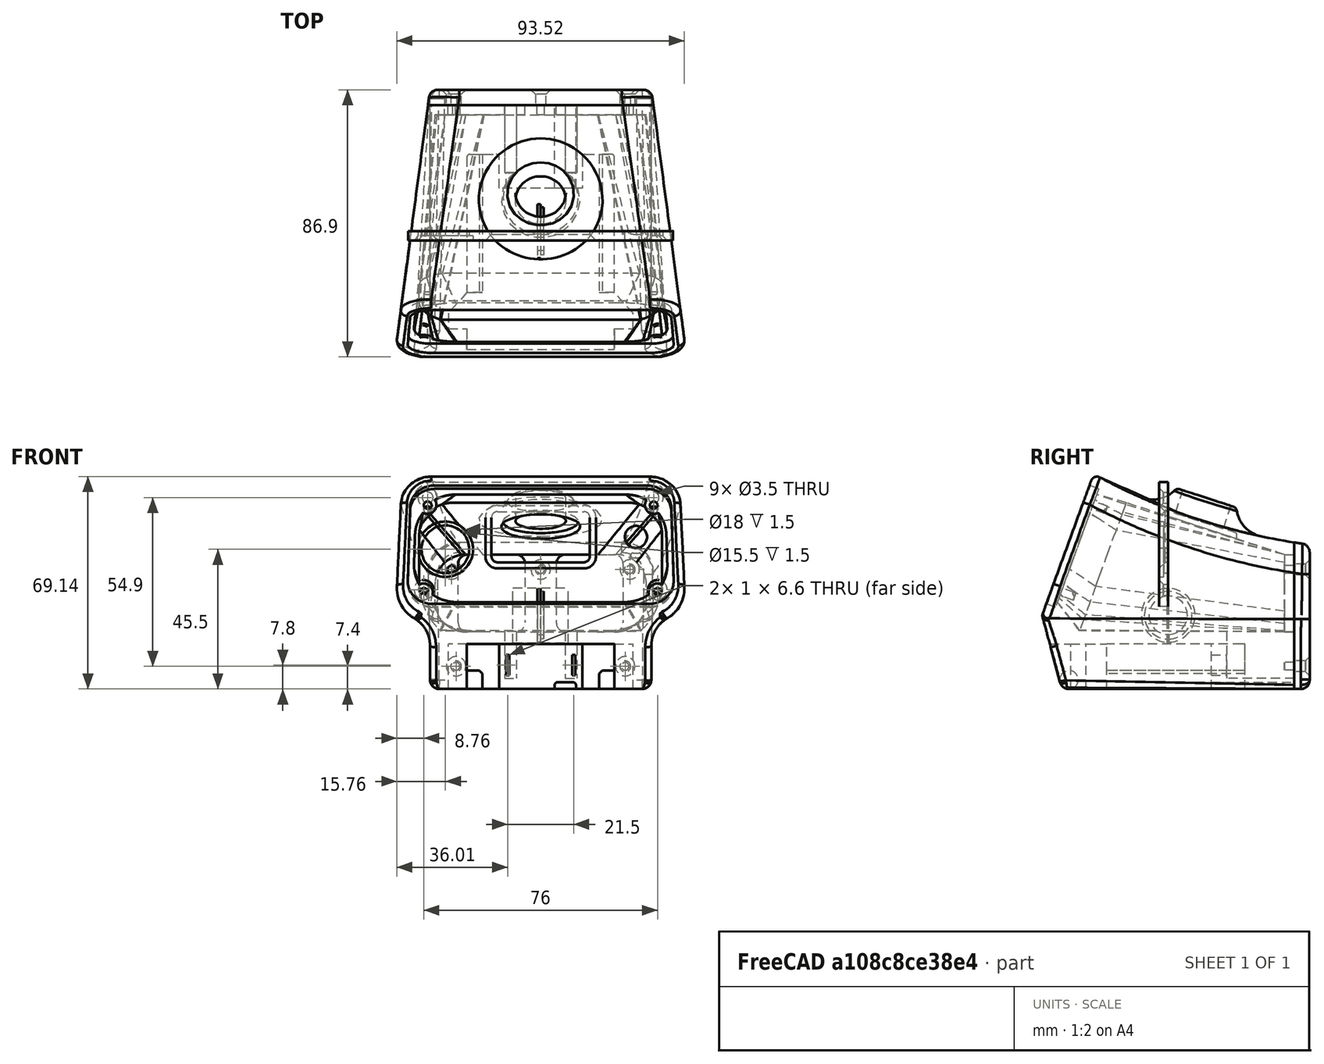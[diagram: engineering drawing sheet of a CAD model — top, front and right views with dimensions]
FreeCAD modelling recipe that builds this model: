
FCSTD DOCUMENT  (FreeCAD 2021.412R24301 +3461 (Git))
Label: solder_station5
License: All rights reserved
LicenseURL: http://en.wikipedia.org/wiki/All_rights_reserved
objects: Sketcher::SketchObject×21, PartDesign::Pocket×10, Part::FeaturePython×6, PartDesign::Fillet×6, App::DocumentObjectGroup×4, PartDesign::Body×4, Mesh::Feature×4, PartDesign::Chamfer×3, PartDesign::FeatureBase×2, PartDesign::Pad×2, PartDesign::Revolution×2, Spreadsheet::Sheet×1, Part::Plane×1, Part::Loft×1, Part::Extrusion×1, Part::MultiCommon×1, PartDesign::SubtractiveLoft×1, PartDesign::Groove×1, Part::Box×1, App::Part×1
note: 115 computed .brp shape members not serialized (recipe doc carries the construction recipe); baked Part::Feature solids carry a one-line shape summary decoded from their .brp

FEATURE [Sketcher::SketchObject] Sketch  label="RearSupport"
  AttachmentOffset = pos=(0,0,-37.8) rot=(0,0,1;0rad)
  FullyConstrained = true
  MapMode = 5
  Placement = pos=(0,37.8,8.4e-15) rot=(1,0,0;1.5708rad)
  Support = -> [XZ_Plane005]
  expr: .AttachmentOffset.Base.z = -<<param>>.mid_depth / 2 + <<param>>.wall
  expr: .Constraints[24] = 3
  expr: .Constraints[37] = <<param>>.bottom_height
  expr: .Constraints[38] = <<param>>.floor
  expr: .Constraints[39] = <<param>>.rear_height - <<param>>.wall
  expr: .Constraints[47] = <<param>>.reart_screw_width2
  expr: .Constraints[48] = <<param>>.rear_screw_width1
  expr: .Constraints[49] = <<param>>.screw_hole
  expr: .Constraints[50] = <<param>>.rear_screw_height
  expr: .Constraints[51] = <<param>>.rear_screw_height
  expr: .Constraints[52] = <<param>>.rear_screw_offset
  sketch-geometry (22):
    g0: LineSegment StartX=-23.8 StartY=19.8 StartZ=0 EndX=-8.1 EndY=19.8 EndZ=0
    g1: LineSegment StartX=26.8 StartY=16.8 StartZ=0 EndX=26.8 EndY=-2.4 EndZ=0
    g2: LineSegment StartX=23.8 StartY=-5.4 StartZ=0 EndX=8.1 EndY=-5.4 EndZ=0
    g3: LineSegment StartX=-26.8 StartY=-2.4 StartZ=0 EndX=-26.8 EndY=16.8 EndZ=0
    g4: LineSegment StartX=-5.1 StartY=16.8 StartZ=0 EndX=-5.1 EndY=-2.4 EndZ=0
    g5: LineSegment StartX=5.1 StartY=16.8 StartZ=0 EndX=5.1 EndY=-2.4 EndZ=0
    g6: LineSegment StartX=8.1 StartY=19.8 StartZ=0 EndX=23.8 EndY=19.8 EndZ=0
    g7: LineSegment StartX=-8.1 StartY=-5.4 StartZ=0 EndX=-23.8 EndY=-5.4 EndZ=0
    g8: ArcOfCircle CenterX=-8.1 CenterY=16.8 CenterZ=0 NormalX=0 NormalY=0 NormalZ=1 AngleXU=0 Radius=3 StartAngle=0 EndAngle=1.5708
    g9: ArcOfCircle CenterX=8.1 CenterY=16.8 CenterZ=0 NormalX=0 NormalY=0 NormalZ=1 AngleXU=0 Radius=3 StartAngle=1.5708 EndAngle=3.14159
    g10: ArcOfCircle CenterX=-8.1 CenterY=-2.4 CenterZ=0 NormalX=0 NormalY=0 NormalZ=1 AngleXU=0 Radius=3 StartAngle=4.71239 EndAngle=6.28319
    g11: ArcOfCircle CenterX=8.1 CenterY=-2.4 CenterZ=0 NormalX=0 NormalY=0 NormalZ=1 AngleXU=0 Radius=3 StartAngle=3.14159 EndAngle=4.71239
    g12: ArcOfCircle CenterX=-23.8 CenterY=16.8 CenterZ=0 NormalX=0 NormalY=0 NormalZ=1 AngleXU=0 Radius=3 StartAngle=1.5708 EndAngle=3.14159
    g13: ArcOfCircle CenterX=-23.8 CenterY=-2.4 CenterZ=0 NormalX=0 NormalY=0 NormalZ=1 AngleXU=0 Radius=3 StartAngle=3.14159 EndAngle=4.71239
    g14: ArcOfCircle CenterX=23.8 CenterY=16.8 CenterZ=0 NormalX=0 NormalY=0 NormalZ=1 AngleXU=0 Radius=3 StartAngle=3e-16 EndAngle=1.5708
    g15: ArcOfCircle CenterX=23.8 CenterY=-2.4 CenterZ=0 NormalX=0 NormalY=0 NormalZ=1 AngleXU=0 Radius=3 StartAngle=4.71239 EndAngle=6.28319
    g16: Circle [constr] CenterX=0 CenterY=-24 CenterZ=0 NormalX=0 NormalY=0 NormalZ=1 AngleXU=0 Radius=3
    g17: Circle CenterX=0 CenterY=14.9 CenterZ=0 NormalX=0 NormalY=0 NormalZ=1 AngleXU=0 Radius=1.25
    g18: Circle CenterX=-29 CenterY=14.9 CenterZ=0 NormalX=0 NormalY=0 NormalZ=1 AngleXU=0 Radius=1.25
    g19: Circle CenterX=-27.5 CenterY=-16.6 CenterZ=0 NormalX=0 NormalY=0 NormalZ=1 AngleXU=0 Radius=1.25
    g20: Circle CenterX=27.5 CenterY=-16.6 CenterZ=0 NormalX=0 NormalY=0 NormalZ=1 AngleXU=0 Radius=1.25
    g21: Circle CenterX=29 CenterY=14.9 CenterZ=0 NormalX=0 NormalY=0 NormalZ=1 AngleXU=0 Radius=1.25
  constraints (53):
    c: Horizontal(g0)
    c: Horizontal(g2)
    c: Vertical(g1)
    c: Vertical(g3)
    c: Vertical(g4)
    c: Vertical(g5)
    c: Tangent(g0,g6)
    c: Tangent(g2,g7)
    c: Tangent(g0,g8) = 1.5708
    c: Tangent(g4,g8) = 1.5708
    c: Tangent(g5,g9) = -1.5708
    c: Tangent(g6,g9) = 1.5708
    c: Tangent(g7,g10) = 1.5708
    c: Tangent(g4,g10) = 1.5708
    c: Tangent(g5,g11) = -1.5708
    c: Tangent(g2,g11) = 1.5708
    c: Tangent(g0,g12) = 1.5708
    c: Tangent(g3,g12) = 1.5708
    c: Tangent(g3,g13) = 1.5708
    c: Tangent(g7,g13) = 1.5708
    c: Tangent(g6,g14) = 1.5708
    c: Tangent(g1,g14) = 1.5708
    c: Tangent(g1,g15) = 1.5708
    c: Tangent(g2,g15) = 1.5708
    c: Radius(g9) = 3
    c: Equal(g12,g13)
    c: Equal(g13,g10)
    c: Equal(g10,g8)
    c: Equal(g11,g15)
    c: Equal(g15,g14)
    c: Equal(g14,g9)
    c: DistanceX(g4,g-1) = 5.1
    c: DistanceX(g5,g1) = 21.7
    c: Symmetric(g4,g5,g-2)
    c: Equal(g7,g2)
    c: PointOnObject(g16,g-2)
    c: Radius(g16) = 3
    c: DistanceY(g16,g-1) = 24
    c: DistanceY(g16,g2) = 18.6
    c: DistanceY(g16,g6) = 43.8
    c: PointOnObject(g17,g-2)
    c: Equal(g21,g18)
    c: Equal(g18,g19)
    c: Equal(g19,g20)
    c: Equal(g18,g17)
    c: Symmetric(g20,g19,g-2)
    c: Symmetric(g18,g21,g-2)
    c: DistanceX(g19,g20) = 55
    c: DistanceX(g18,g21) = 58
    c: Diameter(g19) = 2.5
    c: DistanceY(g20,g21) = 31.5
    c: DistanceY(g20,g17) = 31.5
    c: DistanceY(g16,g19) = 7.4
FEATURE [Spreadsheet::Sheet] Spreadsheet  label="param"
  PythonMode = false
  cells = A1=Body; B2=top_depth; C2(top_depth)=70; B3=mid_depth; C3(mid_depth)=82; D3=half is rear reference; B4=bottom_depth; C4(bottom_depth)=75; B6=bottom_width; C6(bottom_width)=72; B7=bottom_height; C7(bottom_height)=24; B8=bottom_angle; C8(bottom_angle)=15; B10=rear_width; C10(rear_width)=72; B11=rear_height; C11(rear_height)=47; F11=41; B13=mid_width; C13(mid_width)=80; B14=mid_height; C14(mid_height)=56; F14=50; B16=front_width1; C16(front_width1)=92; D16=@top; E16=upper; F16=91; B17=front_width2; C17(front_width2)=95; D17=@mid; E17=lower; F17=94; B18=front_height; C18(front_height)=70; F18=64; B19=front_angle; C19(front_angle)=20; B21=wall; C21(wall)=3.2; B22=radius_big; C22(radius_big)=10; B23=radius_small; C23(radius_small)=3; B24=arch; C24(arch)=200; A26=Button; B27=button_offset; C27(button_offset)=10; B28=button_inside_dia; C28(button_inside_dia)=20; B29=button_outside_dia; C29(button_outside_dia)=22; B30=button_height; C30(button_height)=30.6; F30=26; B31=button_extension; C31(button_extension)=8; B32=button_fillet; C32(button_fillet)=12; B33=button_angle; C33(button_angle)=-18; F33=-17; B34=button_hole; C34(button_hole)=16.4; B35=button_hole_center; C35(button_hole_center)=-0.5; A37=Battery Cuts; B38=batt_carveout; C38(batt_carveout)=14.6; B39=batt_rail; C39(batt_rail)=6; B40=batt_rail_length; C40(batt_rail_length)=45; A42=Terminals; B43=terminal_height; C43(terminal_height)=6.6; B44=terminal_thickness; C44(terminal_thickness)=1; B45=terminal_seperation; C45(terminal_seperation)=21.5; B46=terminal_offset; C46(terminal_offset)=4.5; B47=terminal_depth; C47(terminal_depth)=22; A49=Box Interior; B50=floor; C50(floor)=18.6; B51=rear_inside_width; C51(rear_inside_width)==C10 - C21; D51=calc; B52=rear_inside_height; C52(rear_inside_height)==C11 - C21; D52=calc; B53=mid_inside_width; C53(mid_inside_width)==C13; D53=calc; B54=mid_inside_height; C54(mid_inside_height)==C14 + 7; D54=calc; F54=6; B55=front_inside_width1; C55(front_inside_width1)==C62 - C58 * 2; D55=calc; E55=upper; B56=front_inside_width2; C56(front_inside_width2)==C63 - C58 * 2; D56=calc; E56=lower; B57=front_inside_height; C57(front_inside_height)==C64 - C59 * 2; D57=calc; B58=front_width_lip_width; C58(front_width_lip_width)=3; B59=front_inside_lip_height; C59(front_inside_lip_height)=2; A61=Face; B62=face_width1; C62(face_width1)==84 + 1; B63=face_width2; C63(face_width2)==85.5 + 1; B64=face_height; C64(face_height)=41; F64=35; B65=face_thickness; C65(face_thickness)=3; B66=face_radius; C66(face_radius)=8; B67=face_offset; C67(face_offset)=2.8; F67=2.8; A69=Screws; B70=screw_hole; C70(screw_hole)=2.5; B72=front_screw_width1; C72(front_screw_width1)=73.5; D72=upper; B73=front_screw_width2; C73(front_screw_width2)=76; D73=lower; B74=front_screw_height; C74(front_screw_height)=30; F74=24; B75=front_screw_offset; C75(front_screw_offset)=5.5; B77=rear_screw_width1; C77(rear_screw_width1)=58; B78=reart_screw_width2; C78(reart_screw_width2)=55; B79=rear_screw_height; C79(rear_screw_height)=31.5; F79=25.5; B80=rear_screw_offset; C80(rear_screw_offset)=7.4; A82=Back; B83=back_thickness; C83(back_thickness)=5
FEATURE [Sketcher::SketchObject] Sketch008  label="SketchButtonHole"
  AttachmentOffset = pos=(0,-0.5,30.6) rot=(1,0,0;-0.314159rad)
  FullyConstrained = true
  MapMode = 5
  Placement = pos=(0,-0.5,30.6) rot=(1,0,0;5.96903rad)
  Support = -> [XY_Plane005]
  expr: .AttachmentOffset.Base.y = <<param>>.button_hole_center
  expr: .AttachmentOffset.Base.z = <<param>>.button_height
  expr: .AttachmentOffset.Rotation.Angle = <<param>>.button_angle
  expr: .Constraints[0] = <<param>>.button_hole
  expr: .Constraints[2] = <<param>>.button_offset
  sketch-geometry (1):
    g0: Circle CenterX=0 CenterY=10 CenterZ=0 NormalX=0 NormalY=0 NormalZ=1 AngleXU=0 Radius=8.2
  constraints (3):
    c: Diameter(g0) = 16.4
    c: PointOnObject(g0,g-2)
    c: DistanceY(g-1,g0) = 10
FEATURE [Sketcher::SketchObject] Sketch012  label="SketchSide"
  AttachmentOffset = pos=(2.5,0,0) rot=(0,0,1;0rad)
  FullyConstrained = true
  MapMode = 5
  Placement = pos=(6e-16,2.5,-6e-16) rot=(0.57735,0.57735,0.57735;2.0944rad)
  Support = -> [YZ_Plane006]
  expr: .AttachmentOffset.Base.x = <<param>>.back_thickness / 2
  expr: .Constraints[14] = <<param>>.bottom_height
  expr: .Constraints[15] = <<param>>.radius_small
  expr: .Constraints[16] = 90 - <<param>>.bottom_angle
  expr: .Constraints[17] = 90 - <<param>>.front_angle
  expr: .Constraints[21] = <<param>>.front_height
  expr: .Constraints[4] = <<param>>.rear_height - <<param>>.bottom_height
  expr: .Constraints[5] = <<param>>.arch
  expr: .Constraints[6] = <<param>>.mid_depth + <<param>>.back_thickness
  sketch-geometry (7):
    g0: LineSegment StartX=43.5 StartY=0 StartZ=0 EndX=43.5 EndY=23 EndZ=0
    g1: LineSegment StartX=-43.5 StartY=0 StartZ=0 EndX=-26.7574 EndY=46 EndZ=0
    g2: ArcOfCircle CenterX=69.5235 CenterY=221.3 CenterZ=0 NormalX=0 NormalY=0 NormalZ=1 AngleXU=0 Radius=200 StartAngle=4.21013 EndAngle=4.5819
    g3: LineSegment StartX=-43.5 StartY=0 StartZ=0 EndX=-37.665 EndY=-21.7765 EndZ=0
    g4: LineSegment StartX=-34.7673 StartY=-24 StartZ=0 EndX=43.5 EndY=-24 EndZ=0
    g5: LineSegment StartX=43.5 StartY=-24 StartZ=0 EndX=43.5 EndY=0 EndZ=0
    g6: ArcOfCircle CenterX=-34.7672 CenterY=-21 CenterZ=0 NormalX=0 NormalY=0 NormalZ=1 AngleXU=0 Radius=3 StartAngle=3.4034 EndAngle=4.71238
  constraints (22):
    c: PointOnObject(g1,g-1)
    c: Vertical(g0)
    c: Coincident(g2,g0)
    c: Symmetric(g1,g0,g-2)
    c: DistanceY(g0,g0) = 23
    c: Radius(g2) = 200
    c: DistanceX(g1,g0) = 87
    c: Horizontal(g4)
    c: Coincident(g5,g4)
    c: Vertical(g5)
    c: Coincident(g6,g3)
    c: Coincident(g6,g4)
    c: Tangent(g6,g4)
    c: Tangent(g6,g3)
    c: DistanceY(g4,g-1) = 24
    c: Radius(g6) = 3
    c: Angle(g3,g-1) = 1.309
    c: Angle(g-1,g1) = 1.22173
    c: Coincident(g3,g1)
    c: Coincident(g5,g0)
    c: Coincident(g2,g1)
    c: DistanceY(g4,g1) = 70
FEATURE [Sketcher::SketchObject] Sketch018  label="SketchBat1"
  AttachmentOffset = pos=(0,0,-24) rot=(0,0,1;0rad)
  FullyConstrained = true
  MapMode = 5
  Placement = pos=(0,0,-24) rot=(0,0,1;0rad)
  Support = -> [XY_Plane005]
  expr: .AttachmentOffset.Base.z = -<<param>>.bottom_height
  expr: .Constraints[63] = <<param>>.batt_rail_length
  expr: .Constraints[64] = <<param>>.mid_depth / 2
  sketch-geometry (21):
    g0: LineSegment StartX=-24 StartY=-41.7082 StartZ=0 EndX=24 EndY=-41.7082 EndZ=0
    g1: LineSegment StartX=24 StartY=-41.7082 StartZ=0 EndX=24 EndY=-31.7082 EndZ=0
    g2: LineSegment StartX=24 StartY=-31.7082 StartZ=0 EndX=30 EndY=-31.7082 EndZ=0
    g3: LineSegment StartX=30 StartY=-31.7082 StartZ=0 EndX=30 EndY=-26.7082 EndZ=0
    g4: LineSegment StartX=30 StartY=-26.7082 StartZ=0 EndX=24 EndY=-20 EndZ=0
    g5: LineSegment StartX=24 StartY=-20 StartZ=0 EndX=24 EndY=24 EndZ=0
    g6: LineSegment StartX=13.5 StartY=24 StartZ=0 EndX=13.5 EndY=14 EndZ=0
    g7: LineSegment StartX=13.5 StartY=14 StartZ=0 EndX=-13.5 EndY=14 EndZ=0
    g8: LineSegment StartX=-13.5 StartY=14 StartZ=0 EndX=-13.5 EndY=24 EndZ=0
    g9: LineSegment StartX=-24 StartY=24 StartZ=0 EndX=-24 EndY=-20 EndZ=0
    g10: LineSegment StartX=-24 StartY=-20 StartZ=0 EndX=-30 EndY=-26.7082 EndZ=0
    g11: LineSegment StartX=-30 StartY=-26.7082 StartZ=0 EndX=-30 EndY=-31.7082 EndZ=0
    g12: LineSegment StartX=-30 StartY=-31.7082 StartZ=0 EndX=-24 EndY=-31.7082 EndZ=0
    g13: LineSegment StartX=-24 StartY=-31.7082 StartZ=0 EndX=-24 EndY=-41.7082 EndZ=0
    g14: Circle [constr] CenterX=0 CenterY=41 CenterZ=0 NormalX=0 NormalY=0 NormalZ=1 AngleXU=0 Radius=4
    g15: ArcOfCircle CenterX=-14.5 CenterY=24 CenterZ=0 NormalX=0 NormalY=0 NormalZ=1 AngleXU=0 Radius=1 StartAngle=6.28318 EndAngle=7.85399
    g16: LineSegment StartX=-23 StartY=25 StartZ=0 EndX=-14.5 EndY=25 EndZ=0
    g17: LineSegment StartX=14.5 StartY=25 StartZ=0 EndX=23 EndY=25 EndZ=0
    g18: ArcOfCircle CenterX=-23 CenterY=24 CenterZ=0 NormalX=0 NormalY=0 NormalZ=1 AngleXU=0 Radius=1 StartAngle=1.57079 EndAngle=3.1416
    g19: ArcOfCircle CenterX=14.5 CenterY=24 CenterZ=0 NormalX=0 NormalY=0 NormalZ=1 AngleXU=0 Radius=1 StartAngle=1.5708 EndAngle=3.14159
    g20: ArcOfCircle CenterX=23 CenterY=24 CenterZ=0 NormalX=0 NormalY=0 NormalZ=1 AngleXU=0 Radius=1.00001 StartAngle=2.75124e-06 EndAngle=1.5708
  constraints (65):
    c: Horizontal(g0)
    c: Coincident(g1,g0)
    c: Vertical(g1)
    c: Coincident(g2,g1)
    c: Horizontal(g2)
    c: Coincident(g3,g2)
    c: Coincident(g3,g4)
    c: Vertical(g5)
    c: Coincident(g6,g7)
    c: Coincident(g7,g8)
    c: Vertical(g8)
    c: Vertical(g9)
    c: Coincident(g10,g11)
    c: Vertical(g11)
    c: Coincident(g11,g12)
    c: Horizontal(g12)
    c: Coincident(g12,g13)
    c: Equal(g6,g8)
    c: Equal(g5,g9)
    c: Equal(g4,g10)
    c: Equal(g3,g11)
    c: Equal(g12,g2)
    c: Equal(g1,g13)
    c: Coincident(g13,g0)
    c: Vertical(g13)
    c: DistanceX(g7,g7) = 27
    c: Symmetric(g7,g6,g-2)
    c: Distance(g4) = 9
    c: Vertical(g3)
    c: DistanceY(g3,g3) = 5
    c: DistanceX(g2,g2) = 6
    c: DistanceY(g1,g1) = 10
    c: DistanceX(g0,g0) = 48
    c: PointOnObject(g14,g-2)
    c: Coincident(g9,g10)
    c: Coincident(g5,g4)
    c: Coincident(g15,g8)
    c: Coincident(g16,g15)
    c: Tangent(g15,g8)
    c: Horizontal(g16)
    c: Horizontal(g17)
    c: DistanceX(g9,g5) = 48
    c: Symmetric(g4,g9,g-2)
    c: Equal(g16,g17)
    c: Coincident(g18,g9)
    c: Coincident(g18,g16)
    c: Equal(g18,g15)
    c: Tangent(g18,g16)
    c: Tangent(g18,g9)
    c: DistanceY(g6,g17) = 11
    c: Vertical(g6)
    c: Coincident(g19,g6)
    c: Coincident(g19,g17)
    c: Coincident(g20,g17)
    c: Coincident(g20,g5)
    c: Tangent(g20,g17)
    c: Tangent(g20,g5)
    c: Tangent(g19,g6)
    c: Tangent(g19,g17)
    c: Equal(g15,g19)
    c: Radius(g19) = 1
    c: Radius(g14) = 4
    c: DistanceY(g15,g14) = 16
    c: DistanceY(g9,g16) = 45
    c: DistanceY(g-1,g14) = 41
FEATURE [Sketcher::SketchObject] Sketch019  label="SketchBat2"
  AttachmentOffset = pos=(0,0,-25) rot=(0,0,1;0rad)
  FullyConstrained = true
  MapMode = 5
  Placement = pos=(0,25,5.6e-15) rot=(1,0,0;1.5708rad)
  Support = -> [XZ_Plane005]
  expr: .AttachmentOffset.Base.z = -<<param>>.mid_depth / 2 + 16
  expr: .Constraints[17] = <<param>>.bottom_height
  expr: .Constraints[18] = <<param>>.batt_rail
  expr: .Constraints[19] = 48.01mm
  sketch-geometry (10):
    g0: LineSegment StartX=-24.005 StartY=-18 StartZ=0 EndX=-20.005 EndY=-18 EndZ=0
    g1: LineSegment StartX=-19.005 StartY=-24 StartZ=0 EndX=-24.005 EndY=-24 EndZ=0
    g2: LineSegment StartX=-24.005 StartY=-24 StartZ=0 EndX=-24.005 EndY=-18 EndZ=0
    g3: LineSegment StartX=24.005 StartY=-18 StartZ=0 EndX=20.005 EndY=-18 EndZ=0
    g4: LineSegment StartX=19.005 StartY=-24 StartZ=0 EndX=24.005 EndY=-24 EndZ=0
    g5: LineSegment StartX=24.005 StartY=-24 StartZ=0 EndX=24.005 EndY=-18 EndZ=0
    g6: LineSegment StartX=-19.005 StartY=-19 StartZ=0 EndX=-19.005 EndY=-24 EndZ=0
    g7: LineSegment StartX=19.005 StartY=-24 StartZ=0 EndX=19.005 EndY=-19 EndZ=0
    g8: LineSegment StartX=-20.005 StartY=-18 StartZ=0 EndX=-19.005 EndY=-19 EndZ=0
    g9: LineSegment StartX=19.005 StartY=-19 StartZ=0 EndX=20.005 EndY=-18 EndZ=0
  constraints (29):
    c: Coincident(g1,g2)
    c: Coincident(g2,g0)
    c: Horizontal(g0)
    c: Horizontal(g1)
    c: Vertical(g2)
    c: Coincident(g4,g5)
    c: Coincident(g5,g3)
    c: Horizontal(g3)
    c: Horizontal(g4)
    c: Vertical(g5)
    c: Coincident(g6,g1)
    c: Vertical(g6)
    c: Equal(g1,g4)
    c: Coincident(g7,g4)
    c: Vertical(g7)
    c: Equal(g6,g7)
    c: Symmetric(g1,g4,g-2)
    c: DistanceY(g1,g-1) = 24
    c: DistanceY(g4,g3) = 6
    c: DistanceX(g1,g4) = 48.01
    c: DistanceX(g4,g4) = 5
    c: Coincident(g8,g0)
    c: Coincident(g8,g6)
    c: Coincident(g9,g7)
    c: Coincident(g9,g3)
    c: Equal(g0,g3)
    c: Equal(g2,g5)
    c: DistanceX(g0,g0) = 4
    c: DistanceY(g1,g6) = 5
FEATURE [Sketcher::SketchObject] Sketch021  label="SketchButton"
  AttachmentOffset = pos=(10,30.6,0) rot=(0,0,1;-0.314159rad)
  FullyConstrained = true
  MapMode = 5
  Placement = pos=(-4.6e-15,10,30.6) rot=(-0.506732,-0.697457,-0.506732;4.35963rad)
  Support = -> [YZ_Plane005]
  expr: .AttachmentOffset.Base.x = <<param>>.button_offset
  expr: .AttachmentOffset.Base.y = <<param>>.button_height
  expr: .AttachmentOffset.Rotation.Angle = <<param>>.button_angle
  expr: .Constraints[6] = <<param>>.button_extension
  expr: .Constraints[7] = <<param>>.button_outside_dia / 2
  sketch-geometry (5):
    g0: LineSegment StartX=0 StartY=0 StartZ=0 EndX=0 EndY=8 EndZ=0
    g1: LineSegment StartX=0 StartY=8 StartZ=0 EndX=9 EndY=8 EndZ=0
    g2: LineSegment StartX=0 StartY=0 StartZ=0 EndX=11 EndY=0 EndZ=0
    g3: LineSegment StartX=11 StartY=0 StartZ=0 EndX=11 EndY=6 EndZ=0
    g4: ArcOfCircle CenterX=9 CenterY=6 CenterZ=0 NormalX=0 NormalY=0 NormalZ=1 AngleXU=0 Radius=2 StartAngle=1e-16 EndAngle=1.5708
  constraints (13):
    c: Coincident(g0,g-1)
    c: PointOnObject(g0,g-2)
    c: Coincident(g1,g0)
    c: Horizontal(g1)
    c: Coincident(g2,g0)
    c: Horizontal(g2)
    c: DistanceY(g0,g0) = 8
    c: DistanceX(g2,g2) = 11
    c: Coincident(g3,g2)
    c: Vertical(g3)
    c: Radius(g4) = 2
    c: Tangent(g4,g1) = 1.5708
    c: Tangent(g4,g3) = -1.5708
FEATURE [Sketcher::SketchObject] Sketch022  label="SketchRearInside"
  AttachmentOffset = pos=(0,0,-37.8) rot=(0,0,1;0rad)
  FullyConstrained = true
  MapMode = 5
  Placement = pos=(0,37.8,8.4e-15) rot=(1,0,0;1.5708rad)
  Support = -> [XZ_Plane005]
  expr: .AttachmentOffset.Base.z = -<<param>>.mid_depth / 2 + <<param>>.wall
  expr: .Constraints[12] = <<param>>.radius_big
  expr: .Constraints[18] = <<param>>.rear_inside_width
  expr: .Constraints[26] = <<param>>.bottom_height
  expr: .Constraints[27] = <<param>>.rear_inside_height
  expr: .Constraints[29] = <<param>>.floor
  sketch-geometry (9):
    g0: LineSegment StartX=-34.4 StartY=9.80003 StartZ=0 EndX=-34.4 EndY=4.59997 EndZ=0
    g1: LineSegment StartX=-24.4 StartY=-5.4 StartZ=0 EndX=24.4 EndY=-5.4 EndZ=0
    g2: LineSegment StartX=34.4 StartY=4.59997 StartZ=0 EndX=34.4 EndY=9.80003 EndZ=0
    g3: LineSegment StartX=-24.4 StartY=19.8 StartZ=0 EndX=24.4 EndY=19.8 EndZ=0
    g4: ArcOfCircle CenterX=24.4 CenterY=9.8 CenterZ=0 NormalX=0 NormalY=0 NormalZ=1 AngleXU=0 Radius=10 StartAngle=3.49027e-06 EndAngle=1.57079
    g5: ArcOfCircle CenterX=24.4 CenterY=4.6 CenterZ=0 NormalX=0 NormalY=0 NormalZ=1 AngleXU=0 Radius=10 StartAngle=4.71239 EndAngle=6.28318
    g6: ArcOfCircle CenterX=-24.4 CenterY=9.8 CenterZ=0 NormalX=0 NormalY=0 NormalZ=1 AngleXU=0 Radius=10 StartAngle=1.5708 EndAngle=3.14159
    g7: ArcOfCircle CenterX=-24.4 CenterY=4.6 CenterZ=0 NormalX=0 NormalY=0 NormalZ=1 AngleXU=0 Radius=10 StartAngle=3.1416 EndAngle=4.71239
    g8: Circle [constr] CenterX=0 CenterY=-24 CenterZ=0 NormalX=0 NormalY=0 NormalZ=1 AngleXU=0 Radius=3
  constraints (30):
    c: Vertical(g0)
    c: Horizontal(g1)
    c: Vertical(g2)
    c: Horizontal(g3)
    c: Equal(g3,g1)
    c: Equal(g0,g2)
    c: Coincident(g4,g3)
    c: Coincident(g4,g2)
    c: Coincident(g5,g2)
    c: Coincident(g5,g1)
    c: Coincident(g6,g0)
    c: Coincident(g6,g3)
    c: Radius(g6) = 10
    c: Equal(g6,g4)
    c: Equal(g4,g5)
    c: Coincident(g7,g1)
    c: Coincident(g7,g0)
    c: Equal(g5,g7)
    c: DistanceX(g0,g2) = 68.8
    c: Symmetric(g0,g2,g-2)
    c: Tangent(g4,g2)
    c: Tangent(g4,g3)
    c: Tangent(g5,g2)
    c: Tangent(g5,g1)
    c: Tangent(g6,g3)
    c: PointOnObject(g8,g-2)
    c: DistanceY(g8,g-1) = 24
    c: DistanceY(g8,g3) = 43.8
    c: Radius(g8) = 3
    c: DistanceY(g8,g1) = 18.6
FEATURE [Sketcher::SketchObject] Sketch024  label="SketchFaceCut"
  AttachmentOffset = pos=(0,0,37.6) rot=(1,0,0;-0.349066rad)
  FullyConstrained = true
  MapMode = 5
  Placement = pos=(0,-37.6,-8.3e-15) rot=(-1,0,0;5.06145rad)
  Support = -> [XZ_Plane005]
  expr: .AttachmentOffset.Base.z = <<param>>.mid_depth / 2 - <<param>>.face_thickness - 0.4
  expr: .AttachmentOffset.Rotation.Angle = -<<param>>.front_angle
  expr: .Constraints[13] = <<param>>.face_radius
  expr: .Constraints[22] = <<param>>.face_width1
  expr: .Constraints[23] = <<param>>.face_width2
  expr: .Constraints[24] = <<param>>.face_offset
  expr: .Constraints[25] = <<param>>.face_height
  sketch-geometry (8):
    g0: LineSegment StartX=-34.5035 StartY=43.8 StartZ=0 EndX=34.5037 EndY=43.8 EndZ=0
    g1: LineSegment StartX=42.5001 StartY=36.0399 StartZ=0 EndX=43.25 EndY=11.0399 EndZ=0
    g2: LineSegment StartX=35.2536 StartY=2.8 StartZ=0 EndX=-35.2536 EndY=2.8 EndZ=0
    g3: LineSegment StartX=-43.25 StartY=11.0399 StartZ=0 EndX=-42.4999 EndY=36.0399 EndZ=0
    g4: ArcOfCircle CenterX=34.5037 CenterY=35.8 CenterZ=0 NormalX=0 NormalY=0 NormalZ=1 AngleXU=0 Radius=8 StartAngle=0.0299879 EndAngle=1.5708
    g5: ArcOfCircle CenterX=35.2536 CenterY=10.8 CenterZ=0 NormalX=0 NormalY=0 NormalZ=1 AngleXU=0 Radius=8 StartAngle=4.71239 EndAngle=6.31317
    g6: ArcOfCircle CenterX=-34.5035 CenterY=35.8 CenterZ=0 NormalX=0 NormalY=0 NormalZ=1 AngleXU=0 Radius=8 StartAngle=1.5708 EndAngle=3.1116
    g7: ArcOfCircle CenterX=-35.2536 CenterY=10.8 CenterZ=0 NormalX=0 NormalY=0 NormalZ=1 AngleXU=0 Radius=8 StartAngle=3.1116 EndAngle=4.71239
  constraints (27):
    c: Horizontal(g0)
    c: Coincident(g4,g0)
    c: Coincident(g4,g1)
    c: Coincident(g5,g1)
    c: Coincident(g5,g2)
    c: Coincident(g6,g0)
    c: Coincident(g6,g3)
    c: Coincident(g7,g3)
    c: Coincident(g7,g2)
    c: Equal(g1,g3)
    c: Equal(g4,g6)
    c: Equal(g6,g7)
    c: Equal(g7,g5)
    c: Radius(g4) = 8
    c: Tangent(g6,g3)
    c: Tangent(g7,g3)
    c: Tangent(g7,g2)
    c: Tangent(g6,g0)
    c: Tangent(g4,g0)
    c: Tangent(g4,g1)
    c: Tangent(g5,g1)
    c: Tangent(g5,g2)
    c: DistanceX(g3,g1) = 85
    c: DistanceX(g3,g1) = 86.5
    c: DistanceY(g-1,g2) = 2.8
    c: DistanceY(g2,g0) = 41
    c: Symmetric(g2,g2,g-2)
FEATURE [Sketcher::SketchObject] Sketch025  label="SketchMidInside"
  AttachmentOffset = pos=(0,0,27) rot=(1,0,0;-0.349066rad)
  FullyConstrained = true
  MapMode = 5
  Placement = pos=(0,-27,-6e-15) rot=(-1,0,0;5.06145rad)
  Support = -> [XZ_Plane005]
  expr: .AttachmentOffset.Base.z = <<param>>.mid_depth / 2 - 14
  expr: .AttachmentOffset.Rotation.Angle = -<<param>>.front_angle
  expr: .Constraints[10] = <<param>>.radius_big + 1
  expr: .Constraints[11] = <<param>>.floor
  expr: .Constraints[12] = Spreadsheet.mid_inside_width - 1
  expr: .Constraints[14] = <<param>>.mid_inside_height
  expr: .Constraints[23] = <<param>>.mid_width - 15
  expr: .Constraints[4] = <<param>>.bottom_height
  sketch-geometry (9):
    g0: LineSegment StartX=-28.5 StartY=39 StartZ=0 EndX=28.5 EndY=39 EndZ=0
    g1: LineSegment StartX=39.5 StartY=28 StartZ=0 EndX=39.5 EndY=10 EndZ=0
    g2: LineSegment StartX=32.5 StartY=-5.4 StartZ=0 EndX=-32.5 EndY=-5.4 EndZ=0
    g3: LineSegment StartX=-39.5 StartY=10 StartZ=0 EndX=-39.5 EndY=28 EndZ=0
    g4: Circle [constr] CenterX=0 CenterY=-24 CenterZ=0 NormalX=0 NormalY=0 NormalZ=1 AngleXU=0 Radius=3
    g5: ArcOfCircle CenterX=-28.5 CenterY=28 CenterZ=0 NormalX=0 NormalY=0 NormalZ=1 AngleXU=0 Radius=11 StartAngle=1.5708 EndAngle=3.14159
    g6: ArcOfCircle CenterX=28.5 CenterY=28 CenterZ=0 NormalX=0 NormalY=0 NormalZ=1 AngleXU=0 Radius=11 StartAngle=0 EndAngle=1.5708
    g7: ArcOfCircle CenterX=-15.553 CenterY=11.5941 CenterZ=0 NormalX=0 NormalY=0 NormalZ=1 AngleXU=0 Radius=24 StartAngle=3.20806 EndAngle=3.92838
    g8: ArcOfCircle CenterX=15.553 CenterY=11.5941 CenterZ=0 NormalX=0 NormalY=0 NormalZ=1 AngleXU=0 Radius=24 StartAngle=5.4964 EndAngle=6.21672
  constraints (25):
    c: Vertical(g1)
    c: Vertical(g3)
    c: PointOnObject(g4,g-2)
    c: Radius(g4) = 3
    c: DistanceY(g4,g-1) = 24
    c: Tangent(g3,g5) = 1.5708
    c: Tangent(g0,g5) = 1.5708
    c: Tangent(g0,g6) = 1.5708
    c: Tangent(g1,g6) = 1.5708
    c: Equal(g6,g5)
    c: Radius(g6) = 11
    c: DistanceY(g4,g2) = 18.6
    c: DistanceX(g3,g1) = 79
    c: Symmetric(g2,g2,g-2)
    c: DistanceY(g4,g0) = 63
    c: Symmetric(g0,g0,g-2)
    c: Equal(g3,g1)
    c: Coincident(g7,g2)
    c: Coincident(g8,g1)
    c: Coincident(g8,g2)
    c: Coincident(g7,g3)
    c: Equal(g8,g7)
    c: Radius(g8) = 24
    c: DistanceX(g2,g2) = 65
    c: DistanceY(g1,g1) = 18
FEATURE [Sketcher::SketchObject] Sketch026  label="SketchFrontScrews"
  AttachmentOffset = pos=(0,0,38) rot=(1,0,0;-0.349066rad)
  FullyConstrained = true
  MapMode = 5
  Placement = pos=(0,-38,-8.4e-15) rot=(-1,0,0;5.06145rad)
  Support = -> [XZ_Plane005]
  expr: .AttachmentOffset.Base.z = <<param>>.mid_depth / 2 - <<param>>.face_thickness
  expr: .AttachmentOffset.Rotation.Angle = -<<param>>.front_angle
  expr: .Constraints[0] = <<param>>.front_screw_width1
  expr: .Constraints[13] = <<param>>.screw_hole
  expr: .Constraints[1] = <<param>>.front_screw_width2
  expr: .Constraints[2] = <<param>>.front_screw_height
  expr: .Constraints[9] = <<param>>.face_offset + <<param>>.front_screw_offset
  sketch-geometry (6):
    g0: Circle CenterX=-36.75 CenterY=38.3 CenterZ=0 NormalX=0 NormalY=0 NormalZ=1 AngleXU=0 Radius=1.25
    g1: Circle CenterX=36.75 CenterY=38.3 CenterZ=0 NormalX=0 NormalY=0 NormalZ=1 AngleXU=0 Radius=1.25
    g2: Circle CenterX=-38 CenterY=8.3 CenterZ=0 NormalX=0 NormalY=0 NormalZ=1 AngleXU=0 Radius=1.25
    g3: Circle CenterX=38 CenterY=8.3 CenterZ=0 NormalX=0 NormalY=0 NormalZ=1 AngleXU=0 Radius=1.25
    g4: LineSegment [constr] StartX=-36.75 StartY=38.3 StartZ=0 EndX=36.75 EndY=38.3 EndZ=0
    g5: LineSegment [constr] StartX=-38 StartY=8.3 StartZ=0 EndX=38 EndY=8.3 EndZ=0
  constraints (14):
    c: DistanceX(g0,g1) = 73.5
    c: DistanceX(g2,g3) = 76
    c: DistanceY(g3,g1) = 30
    c: Coincident(g4,g0)
    c: Coincident(g4,g1)
    c: Coincident(g5,g2)
    c: Coincident(g5,g3)
    c: Symmetric(g2,g3,g-2)
    c: Symmetric(g0,g1,g-2)
    c: DistanceY(g-1,g3) = 8.3
    c: Equal(g0,g2)
    c: Equal(g2,g3)
    c: Equal(g3,g1)
    c: Diameter(g0) = 2.5
FEATURE [Sketcher::SketchObject] Sketch023  label="SketchFrontInside"
  AttachmentOffset = pos=(0,0,38) rot=(1,0,0;-0.349066rad)
  ExternalGeometry = -> [Sketch026,Sketch024]
  FullyConstrained = true
  MapMode = 5
  Placement = pos=(0,-38,-8.4e-15) rot=(-1,0,0;5.06145rad)
  Support = -> [XZ_Plane005]
  expr: .AttachmentOffset.Base.z = <<param>>.mid_depth / 2 - <<param>>.face_thickness
  expr: .AttachmentOffset.Rotation.Angle = -<<param>>.front_angle
  sketch-geometry (16):
    g0: LineSegment StartX=-27.5 StartY=4.93681 StartZ=0 EndX=27.5 EndY=4.93681 EndZ=0
    g1: LineSegment StartX=27.5 StartY=41.9368 StartZ=0 EndX=-27.5 EndY=41.9368 EndZ=0
    g2: LineSegment StartX=-40.95 StartY=28.0001 StartZ=0 EndX=-41.25 EndY=18.0001 EndZ=0
    g3: LineSegment StartX=40.95 StartY=28 StartZ=0 EndX=41.25 EndY=18 EndZ=0
    g4: ArcOfCircle CenterX=36.75 CenterY=38.3 CenterZ=0 NormalX=0 NormalY=0 NormalZ=1 AngleXU=0 Radius=3 StartAngle=2.46996 EndAngle=5.23357
    g5: ArcOfCircle CenterX=27.5 CenterY=27.5965 CenterZ=0 NormalX=0 NormalY=0 NormalZ=1 AngleXU=0 Radius=13.4561 StartAngle=0.0299886 EndAngle=0.646116
    g6: ArcOfCircle CenterX=27.5 CenterY=27.5965 CenterZ=0 NormalX=0 NormalY=0 NormalZ=1 AngleXU=0 Radius=14.3403 StartAngle=1.06869 EndAngle=1.5708
    g7: ArcOfCircle CenterX=38 CenterY=8.3 CenterZ=0 NormalX=0 NormalY=0 NormalZ=1 AngleXU=0 Radius=3 StartAngle=1.04133 EndAngle=3.41706
    g8: ArcOfCircle CenterX=27.5 CenterY=17.5875 CenterZ=0 NormalX=0 NormalY=0 NormalZ=1 AngleXU=0 Radius=13.7562 StartAngle=5.77461 EndAngle=6.31317
    g9: ArcOfCircle CenterX=27.5 CenterY=17.5875 CenterZ=0 NormalX=0 NormalY=0 NormalZ=1 AngleXU=0 Radius=12.6507 StartAngle=4.71239 EndAngle=5.35813
    g10: ArcOfCircle CenterX=-36.75 CenterY=38.3 CenterZ=0 NormalX=0 NormalY=0 NormalZ=1 AngleXU=0 Radius=3 StartAngle=4.19123 EndAngle=6.95482
    g11: ArcOfCircle CenterX=-27.5 CenterY=27.5965 CenterZ=0 NormalX=0 NormalY=0 NormalZ=1 AngleXU=0 Radius=13.456 StartAngle=2.49548 EndAngle=3.1116
    g12: ArcOfCircle CenterX=-27.5 CenterY=27.5965 CenterZ=0 NormalX=0 NormalY=0 NormalZ=1 AngleXU=0 Radius=14.3403 StartAngle=1.5708 EndAngle=2.0729
    g13: ArcOfCircle CenterX=-38 CenterY=8.3 CenterZ=0 NormalX=0 NormalY=0 NormalZ=1 AngleXU=0 Radius=3 StartAngle=6.00771 EndAngle=8.38345
    g14: ArcOfCircle CenterX=-27.5 CenterY=17.5875 CenterZ=0 NormalX=0 NormalY=0 NormalZ=1 AngleXU=0 Radius=13.7562 StartAngle=3.1116 EndAngle=3.65016
    g15: ArcOfCircle CenterX=-27.5 CenterY=17.5875 CenterZ=0 NormalX=0 NormalY=0 NormalZ=1 AngleXU=0 Radius=12.6507 StartAngle=4.06665 EndAngle=4.71239
  constraints (42):
    c: Symmetric(g0,g0,g-2)
    c: Symmetric(g1,g1,g-2)
    c: DistanceY(g3,g3) = 10
    c: Equal(g3,g2)
    c: Equal(g1,g0)
    c: DistanceX(g1,g1) = 55
    c: Coincident(g4,g-3)
    c: Coincident(g5,g4)
    c: Coincident(g6,g4)
    c: Radius(g4) = 3
    c: Tangent(g5,g3) = 1.5708
    c: Parallel(g3,g-8)
    c: Tangent(g6,g1) = -1.5708
    c: DistanceX(g3,g-8) = 2
    c: Parallel(g-7,g2)
    c: DistanceX(g-7,g2) = 2
    c: Coincident(g7,g-4)
    c: Coincident(g8,g7)
    c: Coincident(g9,g7)
    c: Tangent(g8,g3) = 1.5708
    c: Tangent(g9,g0) = -1.5708
    c: Coincident(g9,g8)
    c: Coincident(g5,g6)
    c: DistanceY(g-10,g0) = 2
    c: DistanceY(g1,g-9) = 2
    c: Coincident(g10,g-6)
    c: Coincident(g11,g10)
    c: Coincident(g12,g10)
    c: Coincident(g13,g-5)
    c: Coincident(g14,g13)
    c: Coincident(g15,g13)
    c: Tangent(g12,g1) = -1.5708
    c: Tangent(g11,g2) = -1.5708
    c: Coincident(g11,g12)
    c: Coincident(g14,g15)
    c: Tangent(g14,g2) = -1.5708
    c: Tangent(g15,g0) = -1.5708
    c: Equal(g10,g13)
    c: Equal(g13,g7)
    c: Equal(g7,g4)
    c: Equal(g12,g6)
    c: DistanceY(g-1,g3) = 18
FEATURE [Sketcher::SketchObject] Sketch027  label="SketchButtonCarve"
  AttachmentOffset = pos=(10,28.6,0) rot=(0,0,1;-0.314159rad)
  FullyConstrained = true
  MapMode = 5
  Placement = pos=(-4.1e-15,10,28.6) rot=(-0.506732,-0.697457,-0.506732;4.35963rad)
  Support = -> [YZ_Plane005]
  expr: .AttachmentOffset.Base.x = <<param>>.button_offset
  expr: .AttachmentOffset.Base.y = <<param>>.button_height - 2
  expr: .AttachmentOffset.Rotation.Angle = <<param>>.button_angle
  expr: .Constraints[12] = <<param>>.button_hole / 2 + 10
  expr: .Constraints[6] = <<param>>.button_hole / 2 + 4
  sketch-geometry (4):
    g0: LineSegment StartX=0 StartY=2 StartZ=0 EndX=12.2 EndY=2 EndZ=0
    g1: ArcOfCircle CenterX=18.2 CenterY=3.09999 CenterZ=0 NormalX=0 NormalY=0 NormalZ=1 AngleXU=0 Radius=6.09999 StartAngle=3.32291 EndAngle=4.71239
    g2: LineSegment StartX=0 StartY=2 StartZ=0 EndX=0 EndY=-3 EndZ=0
    g3: LineSegment StartX=18.2 StartY=-3 StartZ=0 EndX=0 EndY=-3 EndZ=0
  constraints (13):
    c: Horizontal(g0)
    c: Coincident(g1,g0)
    c: Coincident(g2,g0)
    c: Coincident(g3,g1)
    c: Horizontal(g3)
    c: Tangent(g3,g1)
    c: DistanceX(g0,g0) = 12.2
    c: DistanceY(g2,g2) = 5
    c: Coincident(g2,g3)
    c: Vertical(g2)
    c: PointOnObject(g-1,g2)
    c: DistanceY(g2,g-1) = 3
    c: DistanceX(g3,g3) = 18.2
FEATURE [Sketcher::SketchObject] Sketch028  label="SketchTerminals"
  FullyConstrained = true
  MapMode = 5
  Placement = pos=(0,0,0) rot=(1,0,0;1.5708rad)
  Support = -> [XZ_Plane005]
  expr: .Constraints[18] = <<param>>.terminal_thickness
  expr: .Constraints[19] = <<param>>.terminal_height
  expr: .Constraints[22] = <<param>>.bottom_height
  expr: .Constraints[23] = <<param>>.terminal_offset
  expr: .Constraints[24] = <<param>>.terminal_seperation
  sketch-geometry (15):
    g0: LineSegment StartX=10.25 StartY=-12.9 StartZ=0 EndX=11.25 EndY=-12.9 EndZ=0
    g1: LineSegment StartX=11.25 StartY=-12.9 StartZ=0 EndX=11.25 EndY=-19.5 EndZ=0
    g2: LineSegment StartX=11.25 StartY=-19.5 StartZ=0 EndX=10.25 EndY=-19.5 EndZ=0
    g3: LineSegment StartX=10.25 StartY=-19.5 StartZ=0 EndX=10.25 EndY=-12.9 EndZ=0
    g4: LineSegment StartX=-10.25 StartY=-12.9 StartZ=0 EndX=-11.25 EndY=-12.9 EndZ=0
    g5: LineSegment StartX=-11.25 StartY=-12.9 StartZ=0 EndX=-11.25 EndY=-19.5 EndZ=0
    g6: LineSegment StartX=-11.25 StartY=-19.5 StartZ=0 EndX=-10.25 EndY=-19.5 EndZ=0
    g7: LineSegment StartX=-10.25 StartY=-19.5 StartZ=0 EndX=-10.25 EndY=-12.9 EndZ=0
    g8: Circle [constr] CenterX=0 CenterY=-24 CenterZ=0 NormalX=0 NormalY=0 NormalZ=1 AngleXU=0 Radius=3
    g9: LineSegment StartX=4.5 StartY=-24 StartZ=0 EndX=11.5 EndY=-24 EndZ=0
    g10: LineSegment StartX=11.5 StartY=-24 StartZ=0 EndX=11.5 EndY=-22.8 EndZ=0
    g11: LineSegment StartX=10.5 StartY=-21.8 StartZ=0 EndX=5.5 EndY=-21.8 EndZ=0
    g12: LineSegment StartX=4.5 StartY=-22.8 StartZ=0 EndX=4.5 EndY=-24 EndZ=0
    g13: ArcOfCircle CenterX=5.5 CenterY=-22.8 CenterZ=0 NormalX=0 NormalY=0 NormalZ=1 AngleXU=0 Radius=1 StartAngle=1.5708 EndAngle=3.14159
    g14: ArcOfCircle CenterX=10.5 CenterY=-22.8 CenterZ=0 NormalX=0 NormalY=0 NormalZ=1 AngleXU=0 Radius=1 StartAngle=7e-16 EndAngle=1.5708
  constraints (42):
    c: Coincident(g0,g1)
    c: Coincident(g1,g2)
    c: Coincident(g2,g3)
    c: Coincident(g3,g0)
    c: Horizontal(g0)
    c: Horizontal(g2)
    c: Vertical(g1)
    c: Vertical(g3)
    c: Coincident(g4,g5)
    c: Coincident(g5,g6)
    c: Coincident(g6,g7)
    c: Coincident(g7,g4)
    c: Horizontal(g4)
    c: Horizontal(g6)
    c: Vertical(g5)
    c: Vertical(g7)
    c: Equal(g7,g1)
    c: Equal(g4,g0)
    c: DistanceX(g4,g4) = 1
    c: DistanceY(g3,g3) = 6.6
    c: PointOnObject(g8,g-2)
    c: Radius(g8) = 3
    c: DistanceY(g8,g-1) = 24
    c: DistanceY(g8,g1) = 4.5
    c: DistanceX(g6,g1) = 21.5
    c: Symmetric(g4,g0,g-2)
    c: Coincident(g9,g10)
    c: Coincident(g12,g9)
    c: Horizontal(g9)
    c: Horizontal(g11)
    c: Vertical(g10)
    c: Vertical(g12)
    c: Tangent(g12,g13) = -1.5708
    c: Tangent(g11,g13) = -1.5708
    c: Tangent(g11,g14) = -1.5708
    c: Tangent(g10,g14) = -1.5708
    c: DistanceX(g9,g9) = 7
    c: DistanceY(g9,g11) = 2.2
    c: DistanceX(g8,g9) = 4.5
    c: Equal(g13,g14)
    c: Radius(g14) = 1
    c: DistanceY(g8,g9) = 0
FEATURE [Sketcher::SketchObject] Sketch029  label="SketchAccess"
  AttachmentOffset = pos=(0,0,-41) rot=(0,0,1;0rad)
  FullyConstrained = true
  MapMode = 5
  Placement = pos=(0,41,9.1e-15) rot=(1,0,0;1.5708rad)
  Support = -> [XZ_Plane005]
  expr: .AttachmentOffset.Base.z = -<<param>>.mid_depth / 2
  expr: .Constraints[17] = <<param>>.terminal_seperation + <<param>>.terminal_thickness * 2
  expr: .Constraints[25] = <<param>>.terminal_offset - 1
  expr: .Constraints[5] = <<param>>.bottom_height
  sketch-geometry (9):
    g0: LineSegment StartX=-11.75 StartY=-0.5 StartZ=0 EndX=-11.75 EndY=-20.5 EndZ=0
    g1: LineSegment StartX=-7.95 StartY=-0.5 StartZ=0 EndX=-7.95 EndY=-20.5 EndZ=0
    g2: LineSegment StartX=7.95 StartY=-0.5 StartZ=0 EndX=7.95 EndY=-20.5 EndZ=0
    g3: LineSegment StartX=11.75 StartY=-0.5 StartZ=0 EndX=11.75 EndY=-20.5 EndZ=0
    g4: Circle [constr] CenterX=0 CenterY=-24 CenterZ=0 NormalX=0 NormalY=0 NormalZ=1 AngleXU=0 Radius=3
    g5: LineSegment StartX=-11.75 StartY=-20.5 StartZ=0 EndX=-7.95 EndY=-20.5 EndZ=0
    g6: LineSegment StartX=-11.75 StartY=-0.5 StartZ=0 EndX=-7.95 EndY=-0.5 EndZ=0
    g7: LineSegment StartX=7.95 StartY=-0.5 StartZ=0 EndX=11.75 EndY=-0.5 EndZ=0
    g8: LineSegment StartX=7.95 StartY=-20.5 StartZ=0 EndX=11.75 EndY=-20.5 EndZ=0
  constraints (26):
    c: Vertical(g0)
    c: Vertical(g2)
    c: Equal(g1,g2)
    c: PointOnObject(g4,g-2)
    c: Radius(g4) = 3
    c: DistanceY(g4,g-1) = 24
    c: Coincident(g5,g0)
    c: Coincident(g5,g1)
    c: Coincident(g6,g0)
    c: Coincident(g6,g1)
    c: Horizontal(g6)
    c: Coincident(g7,g2)
    c: Coincident(g7,g3)
    c: Horizontal(g7)
    c: Coincident(g8,g2)
    c: Coincident(g8,g3)
    c: Horizontal(g8)
    c: DistanceX(g0,g3) = 23.5
    c: Vertical(g3)
    c: Equal(g7,g6)
    c: DistanceY(g3,g3) = 20
    c: Symmetric(g1,g2,g-2)
    c: DistanceX(g6,g6) = 3.8
    c: Vertical(g1)
    c: Horizontal(g5)
    c: DistanceY(g4,g1) = 3.5
FEATURE [Sketcher::SketchObject] Sketch030  label="SketchFront"
  AttachmentOffset = pos=(0,0,41) rot=(0,0,1;0rad)
  FullyConstrained = true
  MapMode = 5
  Placement = pos=(0,-41,-9.1e-15) rot=(1,0,0;1.5708rad)
  Support = -> [XZ_Plane006]
  expr: .AttachmentOffset.Base.z = <<param>>.mid_depth / 2
  expr: .Constraints[10] = <<param>>.front_width2
  expr: .Constraints[11] = <<param>>.front_width2
  expr: .Constraints[12] = <<param>>.front_height + 2
  expr: .Constraints[22] = <<param>>.radius_big * 1.2
  expr: .Constraints[27] = <<param>>.radius_big
  expr: .Constraints[6] = <<param>>.radius_small
  expr: .Constraints[7] = <<param>>.bottom_width
  expr: .Constraints[9] = <<param>>.bottom_height
  sketch-geometry (12):
    g0: LineSegment StartX=-47.5 StartY=48 StartZ=0 EndX=47.5 EndY=48 EndZ=0
    g1: LineSegment StartX=47.5 StartY=48 StartZ=0 EndX=47.5 EndY=9.54506 EndZ=0
    g2: LineSegment StartX=36 StartY=-9.78755 StartZ=0 EndX=36 EndY=-21 EndZ=0
    g3: LineSegment StartX=33 StartY=-24 StartZ=0 EndX=-33 EndY=-24 EndZ=0
    g4: LineSegment StartX=-36 StartY=-21 StartZ=0 EndX=-36 EndY=-9.78755 EndZ=0
    g5: LineSegment StartX=-47.5 StartY=9.54506 StartZ=0 EndX=-47.5 EndY=48 EndZ=0
    g6: ArcOfCircle CenterX=-33 CenterY=-21 CenterZ=0 NormalX=0 NormalY=0 NormalZ=1 AngleXU=0 Radius=3 StartAngle=3.14159 EndAngle=4.71239
    g7: ArcOfCircle CenterX=33 CenterY=-21 CenterZ=0 NormalX=0 NormalY=0 NormalZ=1 AngleXU=0 Radius=3 StartAngle=4.71239 EndAngle=6.28319
    g8: ArcOfCircle CenterX=46 CenterY=-9.78755 CenterZ=0 NormalX=0 NormalY=0 NormalZ=1 AngleXU=0 Radius=10 StartAngle=2.06834 EndAngle=3.14159
    g9: ArcOfCircle CenterX=35.5 CenterY=9.54506 CenterZ=0 NormalX=0 NormalY=0 NormalZ=1 AngleXU=0 Radius=12 StartAngle=5.20994 EndAngle=6.28319
    g10: ArcOfCircle CenterX=-46 CenterY=-9.78755 CenterZ=0 NormalX=0 NormalY=0 NormalZ=1 AngleXU=0 Radius=10 StartAngle=0 EndAngle=1.07325
    g11: ArcOfCircle CenterX=-35.5 CenterY=9.54506 CenterZ=0 NormalX=0 NormalY=0 NormalZ=1 AngleXU=0 Radius=12 StartAngle=3.14159 EndAngle=4.21484
  constraints (30):
    c: Vertical(g2)
    c: Vertical(g4)
    c: Tangent(g4,g6) = 1.5708
    c: Tangent(g3,g6) = 1.5708
    c: Tangent(g3,g7) = 1.5708
    c: Tangent(g2,g7) = 1.5708
    c: Radius(g7) = 3
    c: DistanceX(g4,g2) = 72
    c: Symmetric(g3,g3,g-2)
    c: DistanceY(g3,g-1) = 24
    c: DistanceX(g5,g1) = 95
    c: DistanceX(g5,g1) = 95
    c: DistanceY(g3,g0) = 72
    c: Equal(g7,g6)
    c: Equal(g10,g8)
    c: Symmetric(g5,g1,g-2)
    c: Equal(g4,g2)
    c: Coincident(g8,g2)
    c: Coincident(g0,g1)
    c: Coincident(g5,g0)
    c: Symmetric(g0,g0,g-2)
    c: Equal(g9,g11)
    c: Radius(g9) = 12
    c: Tangent(g11,g5) = 1.5708
    c: Tangent(g1,g9) = 1.5708
    c: Tangent(g11,g10) = 1.5708
    c: Tangent(g8,g9) = 1.5708
    c: Radius(g8) = 10
    c: DistanceY(g8,g-1) = 1
    c: Tangent(g10,g4) = -1.5708
FEATURE [Sketcher::SketchObject] Sketch031  label="SketchRear"
  AttachmentOffset = pos=(0,0,-46) rot=(0,0,1;0rad)
  FullyConstrained = true
  MapMode = 5
  Placement = pos=(0,46,1.02e-14) rot=(1,0,0;1.5708rad)
  Support = -> [XZ_Plane006]
  expr: .AttachmentOffset.Base.z = -<<param>>.mid_depth / 2 - <<param>>.back_thickness
  expr: .Constraints[15] = <<param>>.front_height + 2
  expr: .Constraints[1] = <<param>>.radius_small
  expr: .Constraints[2] = <<param>>.bottom_height
  expr: .Constraints[3] = <<param>>.rear_width
  sketch-geometry (6):
    g0: LineSegment StartX=-33 StartY=-24 StartZ=0 EndX=33 EndY=-24 EndZ=0
    g1: LineSegment StartX=36 StartY=48 StartZ=0 EndX=-36 EndY=48 EndZ=0
    g2: ArcOfCircle CenterX=-33 CenterY=-21 CenterZ=0 NormalX=0 NormalY=0 NormalZ=1 AngleXU=0 Radius=3 StartAngle=3.14159 EndAngle=4.71239
    g3: ArcOfCircle CenterX=33 CenterY=-21 CenterZ=0 NormalX=0 NormalY=0 NormalZ=1 AngleXU=0 Radius=3 StartAngle=4.71239 EndAngle=6.28319
    g4: LineSegment StartX=36 StartY=-21 StartZ=0 EndX=36 EndY=48 EndZ=0
    g5: LineSegment StartX=-36 StartY=-21 StartZ=0 EndX=-36 EndY=48 EndZ=0
  constraints (19):
    c: Horizontal(g0)
    c: Radius(g3) = 3
    c: DistanceY(g0,g-1) = 24
    c: DistanceX(g2,g3) = 72
    c: Coincident(g4,g3)
    c: Vertical(g4)
    c: Coincident(g5,g2)
    c: Equal(g5,g4)
    c: Horizontal(g3,g3)
    c: Horizontal(g2,g2)
    c: Equal(g2,g3)
    c: Coincident(g0,g2)
    c: Coincident(g0,g3)
    c: Vertical(g2,g0)
    c: Vertical(g5)
    c: DistanceY(g0,g1) = 72
    c: Symmetric(g4,g5,g-2)
    c: Coincident(g4,g1)
    c: Coincident(g5,g1)
FEATURE [Part::Plane] Plane002  label="Plane"
  AttacherType = Attacher::AttachEngine3D
  Length = 152
  Placement = pos=(-75,41,-75) rot=(1,0,0;1.5708rad)
  Support = -> [XZ_Plane006]
  Width = 150
  expr: .Placement.Base.y = <<param>>.mid_depth / 2
FEATURE [Sketcher::SketchObject] Sketch032  label="SketchBack"
  FullyConstrained = true
  MapMode = 5
  Placement = pos=(0,0,0) rot=(1,0,0;1.5708rad)
  Support = -> [XZ_Plane]
  expr: .Constraints[10] = <<param>>.rear_screw_width1
  expr: .Constraints[11] = <<param>>.reart_screw_width2
  expr: .Constraints[12] = <<param>>.rear_screw_height
  expr: .Constraints[15] = <<param>>.rear_screw_offset
  expr: .Constraints[1] = <<param>>.bottom_height
  expr: .Constraints[2] = <<param>>.rear_width
  expr: .Constraints[9] = <<param>>.screw_hole + 1
  sketch-geometry (6):
    g0: LineSegment [constr] StartX=36 StartY=-24 StartZ=0 EndX=-36 EndY=-24 EndZ=0
    g1: Circle CenterX=-29 CenterY=14.9 CenterZ=0 NormalX=0 NormalY=0 NormalZ=1 AngleXU=0 Radius=1.75
    g2: Circle CenterX=0 CenterY=14.9 CenterZ=0 NormalX=0 NormalY=0 NormalZ=1 AngleXU=0 Radius=1.75
    g3: Circle CenterX=29 CenterY=14.9 CenterZ=0 NormalX=0 NormalY=0 NormalZ=1 AngleXU=0 Radius=1.75
    g4: Circle CenterX=-27.5 CenterY=-16.6 CenterZ=0 NormalX=0 NormalY=0 NormalZ=1 AngleXU=0 Radius=1.75
    g5: Circle CenterX=27.5 CenterY=-16.6 CenterZ=0 NormalX=0 NormalY=0 NormalZ=1 AngleXU=0 Radius=1.75
  constraints (16):
    c: Symmetric(g0,g0,g-2)
    c: DistanceY(g0,g-1) = 24
    c: DistanceX(g0,g0) = 72
    c: Symmetric(g1,g3,g-2)
    c: Symmetric(g4,g5,g-2)
    c: Equal(g4,g1)
    c: Equal(g1,g2)
    c: Equal(g2,g3)
    c: Equal(g3,g5)
    c: Diameter(g1) = 3.5
    c: DistanceX(g1,g3) = 58
    c: DistanceX(g4,g5) = 55
    c: DistanceY(g5,g3) = 31.5
    c: Horizontal(g1,g2)
    c: PointOnObject(g2,g-2)
    c: DistanceY(g0,g5) = 7.4
FEATURE [Part::Loft] Loft
  Closed = false
  MaxDegree = 5
  Ruled = false
  Sections = -> [Sketch030,Sketch031]
  Solid = true
FEATURE [Part::Extrusion] Extrude
  Base = -> Sketch012
  Dir = (1,-1e-16,1e-16)
  DirMode = 2
  FaceMakerClass = Part::FaceMakerBullseye
  InnerTaperAngle = 0
  InnerTaperAngleRev = 0
  LengthFwd = 100
  LengthRev = 0
  Solid = true
  Symmetric = true
FEATURE [Part::MultiCommon] Common
  Shapes = -> [Extrude,Loft]
FEATURE [Part::FeaturePython] Slice  # WARN: FeaturePython — macro-defined, semantics opaque (R4)
  Base = -> Common
  Mode = 1
  Tolerance = 0
  Tools = -> [Plane002]
FEATURE [Part::FeaturePython] Slice_child0  label="Slice.0"  # WARN: FeaturePython — macro-defined, semantics opaque (R4)
  Base = -> Slice
  FilterType = 1
  Invert = false
  OverrideMaxVal = 0
  WindowFrom = 80
  WindowTo = 100
  items = 0
FEATURE [Part::FeaturePython] Slice_child1  label="Slice.1"  # WARN: FeaturePython — macro-defined, semantics opaque (R4)
  Base = -> Slice
  FilterType = 1
  Invert = false
  OverrideMaxVal = 0
  WindowFrom = 80
  WindowTo = 100
  items = 1
FEATURE [App::DocumentObjectGroup] GrExplode_Slice  label="Exploded Slice"
  ExportMode = 1
  Group = -> [Slice_child0,Slice_child1]
  _GroupVersion = 1
FEATURE [App::DocumentObjectGroup] Group001  label="BaseShape"
  ExportMode = 1
  Group = -> [Common,Sketch012,Sketch031,Sketch030,Plane002,GrExplode_Slice]
  _GroupVersion = 1
FEATURE [PartDesign::FeatureBase] BaseFeature
  BaseFeature = -> Slice_child1
  NewSolid = false
  Suppress = false
FEATURE [PartDesign::Pocket] Pocket
  BaseFeature = -> BaseFeature
  ClaimChildren = false
  Fit = 0
  FitJoin = 0
  InnerFit = 0
  InnerFitJoin = 0
  InnerTaperAngle = 0
  InnerTaperAngleRev = 0
  Length = 5
  Length2 = 100
  Midplane = true
  NewSolid = false
  Profile = -> Sketch032
  Suppress = false
  Type = 1
FEATURE [PartDesign::FeatureBase] BaseFeature001
  BaseFeature = -> Slice_child0
  NewSolid = false
  Suppress = false
FEATURE [PartDesign::Pocket] Pocket001  label="PocketBatt"
  BaseFeature = -> BaseFeature001
  ClaimChildren = false
  Fit = 0
  FitJoin = 0
  InnerFit = 0
  InnerFitJoin = 0
  InnerTaperAngle = 0
  InnerTaperAngleRev = 0
  Length = 14.6
  Length2 = 100
  NewSolid = false
  Profile = -> Sketch018
  Reversed = true
  Suppress = false
  Type = 0
  expr: Length = <<param>>.batt_carveout
FEATURE [PartDesign::Pad] Pad  label="PadBatt"
  BaseFeature = -> Pocket001
  ClaimChildren = false
  Direction = (1,1,1)
  Fit = 0
  FitJoin = 0
  InnerFit = 0
  InnerFitJoin = 0
  InnerTaperAngle = 0
  InnerTaperAngleRev = 0
  Length = 45
  Length2 = 100
  NewSolid = false
  Profile = -> Sketch019
  Suppress = false
  Type = 0
  expr: Length = <<param>>.batt_rail_length
FEATURE [PartDesign::Pocket] Pocket002  label="PocketSupport"
  BaseFeature = -> Pad
  ClaimChildren = false
  Fit = 0
  FitJoin = 0
  InnerFit = 0
  InnerFitJoin = 0
  InnerTaperAngle = 0
  InnerTaperAngleRev = 0
  Length = 5
  Length2 = 100
  NewSolid = false
  Profile = -> Sketch
  Suppress = false
  Type = 0
FEATURE [PartDesign::Pocket] Pocket006  label="PocketTerminal"
  BaseFeature = -> Pocket002
  ClaimChildren = false
  Fit = 0
  FitJoin = 0
  InnerFit = 0
  InnerFitJoin = 0
  InnerTaperAngle = 0
  InnerTaperAngleRev = 0
  Length = 5
  Length2 = 100
  Midplane = true
  NewSolid = false
  Profile = -> Sketch028
  Suppress = false
  Type = 1
FEATURE [PartDesign::Pocket] Pocket005  label="PocketAccess"
  BaseFeature = -> Pocket006
  ClaimChildren = false
  Fit = 0
  FitJoin = 0
  InnerFit = 0
  InnerFitJoin = 0
  InnerTaperAngle = 0
  InnerTaperAngleRev = 0
  Length = 22
  Length2 = 100
  NewSolid = false
  Profile = -> Sketch029
  Reversed = true
  Suppress = false
  Type = 0
  expr: Length = <<param>>.terminal_depth
FEATURE [PartDesign::SubtractiveLoft] SubtractiveLoft
  BaseFeature = -> Pocket005
  ClaimChildren = false
  Closed = false
  Fit = 0
  FitJoin = 0
  InnerFit = 0
  InnerFitJoin = 0
  NewSolid = false
  Profile = -> Sketch022
  Ruled = true
  Sections = -> [Sketch025,Sketch023]
  Suppress = false
FEATURE [PartDesign::Revolution] Revolution  label="RevolutionButton"
  Angle = 360
  Axis = (-1e-16,0.309017,0.951057)
  Base = (-4.6e-15,10,30.6)
  BaseFeature = -> SubtractiveLoft
  ClaimChildren = false
  Fit = 0
  FitJoin = 0
  InnerFit = 0
  InnerFitJoin = 0
  NewSolid = false
  Profile = -> Sketch021
  ReferenceAxis = -> Sketch021 [V_Axis]
  Reversed = true
  Suppress = false
FEATURE [PartDesign::Pocket] Pocket007  label="PocketButton"
  BaseFeature = -> Revolution
  ClaimChildren = false
  Fit = 0
  FitJoin = 0
  InnerFit = 0
  InnerFitJoin = 0
  InnerTaperAngle = 0
  InnerTaperAngleRev = 0
  Length = 14
  Length2 = 100
  NewSolid = false
  Profile = -> Sketch008
  Reversed = true
  Suppress = false
  Type = 0
FEATURE [PartDesign::Groove] Groove  label="GrooveButton"
  Angle = 360
  Axis = (-1e-16,0.309017,0.951057)
  Base = (-4.1e-15,10,28.6)
  BaseFeature = -> Pocket007
  ClaimChildren = false
  Fit = 0
  FitJoin = 0
  InnerFit = 0
  InnerFitJoin = 0
  NewSolid = false
  Profile = -> Sketch027
  ReferenceAxis = -> Sketch027 [V_Axis]
  Suppress = false
FEATURE [PartDesign::Pocket] Pocket004  label="PocketFrontScrews"
  BaseFeature = -> Groove
  ClaimChildren = false
  Fit = 0
  FitJoin = 0
  InnerFit = 0
  InnerFitJoin = 0
  InnerTaperAngle = 0
  InnerTaperAngleRev = 0
  Length = 5
  Length2 = 100
  NewSolid = false
  Profile = -> Sketch026
  Suppress = false
  Type = 0
FEATURE [PartDesign::Pocket] Pocket003  label="PocketFace"
  BaseFeature = -> Pocket004
  ClaimChildren = false
  Fit = 0
  FitJoin = 0
  InnerFit = 0
  InnerFitJoin = 0
  InnerTaperAngle = 0
  InnerTaperAngleRev = 0
  Length = 6
  Length2 = 100
  NewSolid = false
  Profile = -> Sketch024
  Reversed = true
  Suppress = false
  Type = 0
  expr: Length = <<param>>.face_thickness * 2
FEATURE [Sketcher::SketchObject] Sketch033  label="SketchFace"
  FullyConstrained = true
  MapMode = 5
  Placement = pos=(0,0,0) rot=(1,0,0;1.5708rad)
  Support = -> [XZ_Plane007]
  expr: .Constraints[12] = <<param>>.face_radius
  expr: .Constraints[21] = <<param>>.face_width1 - 0.4
  expr: .Constraints[22] = <<param>>.face_width2 - 0.4
  expr: .Constraints[23] = <<param>>.face_height - 0.4
  expr: .Constraints[27] = <<param>>.screw_hole + 1
  expr: .Constraints[28] = <<param>>.front_screw_width2 / 2
  expr: .Constraints[29] = <<param>>.front_screw_width2 / 2
  expr: .Constraints[30] = <<param>>.front_screw_width1 / 2
  expr: .Constraints[31] = <<param>>.front_screw_width1 / 2
  expr: .Constraints[32] = <<param>>.front_screw_height
  expr: .Constraints[35] = <<param>>.front_screw_offset + <<param>>.face_offset
  expr: .Constraints[48] = <<param>>.face_offset
  sketch-geometry (23):
    g0: LineSegment StartX=-34.3037 StartY=43.4 StartZ=0 EndX=34.3037 EndY=43.4 EndZ=0
    g1: LineSegment StartX=42.3 StartY=35.6438 StartZ=0 EndX=43.05 EndY=11.0438 EndZ=0
    g2: LineSegment StartX=35.0537 StartY=2.8 StartZ=0 EndX=-35.0537 EndY=2.8 EndZ=0
    g3: LineSegment StartX=-43.05 StartY=11.0438 StartZ=0 EndX=-42.3 EndY=35.6438 EndZ=0
    g4: ArcOfCircle CenterX=34.3037 CenterY=35.4 CenterZ=0 NormalX=0 NormalY=0 NormalZ=1 AngleXU=0 Radius=8 StartAngle=0.0304753 EndAngle=1.5708
    g5: ArcOfCircle CenterX=35.0537 CenterY=10.8 CenterZ=0 NormalX=0 NormalY=0 NormalZ=1 AngleXU=0 Radius=8 StartAngle=4.71239 EndAngle=6.31366
    g6: ArcOfCircle CenterX=-34.3037 CenterY=35.4 CenterZ=0 NormalX=0 NormalY=0 NormalZ=1 AngleXU=0 Radius=8 StartAngle=1.5708 EndAngle=3.11112
    g7: ArcOfCircle CenterX=-35.0537 CenterY=10.8 CenterZ=0 NormalX=0 NormalY=0 NormalZ=1 AngleXU=0 Radius=8 StartAngle=3.11111 EndAngle=4.71239
    g8: Circle CenterX=-36.75 CenterY=38.3 CenterZ=0 NormalX=0 NormalY=0 NormalZ=1 AngleXU=0 Radius=1.75
    g9: Circle CenterX=36.75 CenterY=38.3 CenterZ=0 NormalX=0 NormalY=0 NormalZ=1 AngleXU=0 Radius=1.75
    g10: Circle CenterX=-38 CenterY=8.3 CenterZ=0 NormalX=0 NormalY=0 NormalZ=1 AngleXU=0 Radius=1.75
    g11: Circle CenterX=38 CenterY=8.3 CenterZ=0 NormalX=0 NormalY=0 NormalZ=1 AngleXU=0 Radius=1.75
    g12: LineSegment StartX=-14 StartY=33.75 StartZ=0 EndX=14 EndY=33.75 EndZ=0
    g13: LineSegment StartX=16 StartY=31.75 StartZ=0 EndX=16 EndY=19.25 EndZ=0
    g14: LineSegment StartX=14 StartY=17.25 StartZ=0 EndX=-14 EndY=17.25 EndZ=0
    g15: LineSegment StartX=-16 StartY=19.25 StartZ=0 EndX=-16 EndY=31.75 EndZ=0
    g16: ArcOfCircle CenterX=-14 CenterY=31.75 CenterZ=0 NormalX=0 NormalY=0 NormalZ=1 AngleXU=0 Radius=2 StartAngle=1.5708 EndAngle=3.14159
    g17: ArcOfCircle CenterX=-14 CenterY=19.25 CenterZ=0 NormalX=0 NormalY=0 NormalZ=1 AngleXU=0 Radius=2 StartAngle=3.14159 EndAngle=4.71239
    g18: ArcOfCircle CenterX=14 CenterY=19.25 CenterZ=0 NormalX=0 NormalY=0 NormalZ=1 AngleXU=0 Radius=2 StartAngle=4.71239 EndAngle=6.28319
    g19: ArcOfCircle CenterX=14 CenterY=31.75 CenterZ=0 NormalX=0 NormalY=0 NormalZ=1 AngleXU=0 Radius=2 StartAngle=7e-16 EndAngle=1.5708
    g20: Circle CenterX=-31 CenterY=21.5 CenterZ=0 NormalX=0 NormalY=0 NormalZ=1 AngleXU=0 Radius=7.75
    g21: Circle CenterX=31 CenterY=25.5 CenterZ=0 NormalX=0 NormalY=0 NormalZ=1 AngleXU=0 Radius=3.6
    g22: LineSegment [constr] StartX=-69 StartY=25.5 StartZ=0 EndX=31 EndY=25.5 EndZ=0
  constraints (67):
    c: Coincident(g4,g0)
    c: Coincident(g4,g1)
    c: Coincident(g5,g1)
    c: Coincident(g5,g2)
    c: Coincident(g6,g0)
    c: Coincident(g6,g3)
    c: Coincident(g7,g3)
    c: Coincident(g7,g2)
    c: Equal(g1,g3)
    c: Equal(g4,g6)
    c: Equal(g6,g7)
    c: Equal(g7,g5)
    c: Radius(g4) = 8
    c: Tangent(g6,g3)
    c: Tangent(g7,g3)
    c: Tangent(g7,g2)
    c: Tangent(g6,g0)
    c: Tangent(g4,g0)
    c: Tangent(g4,g1)
    c: Tangent(g5,g1)
    c: Tangent(g5,g2)
    c: DistanceX(g3,g1) = 84.6
    c: DistanceX(g3,g1) = 86.1
    c: DistanceY(g2,g0) = 40.6
    c: Equal(g9,g8)
    c: Equal(g8,g10)
    c: Equal(g10,g11)
    c: Diameter(g8) = 3.5
    c: DistanceX(g10,g-1) = 38
    c: DistanceX(g-1,g11) = 38
    c: DistanceX(g-1,g9) = 36.75
    c: DistanceX(g8,g-1) = 36.75
    c: DistanceY(g11,g9) = 30
    c: Horizontal(g8,g9)
    c: Horizontal(g10,g11)
    c: DistanceY(g-1,g11) = 8.3
    c: Horizontal(g12)
    c: Horizontal(g14)
    c: Vertical(g13)
    c: Vertical(g15)
    c: Tangent(g15,g16) = 1.5708
    c: Tangent(g12,g16) = 1.5708
    c: Tangent(g15,g17) = 1.5708
    c: Tangent(g14,g17) = 1.5708
    c: Tangent(g14,g18) = 1.5708
    c: Tangent(g13,g18) = 1.5708
    c: Tangent(g12,g19) = 1.5708
    c: Tangent(g13,g19) = 1.5708
    c: DistanceY(g-1,g2) = 2.8
    c: Horizontal(g0)
    c: Symmetric(g2,g2,g-2)
    c: Diameter(g20) = 15.5
    c: Diameter(g21) = 7.2
    c: Equal(g16,g17)
    c: Equal(g17,g18)
    c: Equal(g18,g19)
    c: DistanceY(g14,g12) = 16.5
    c: DistanceX(g15,g13) = 32
    c: Radius(g19) = 2
    c: DistanceX(g20,g21) = 62
    c: DistanceX(g13,g21) = 15
    c: Symmetric(g12,g14,g22)
    c: DistanceY(g20,g22) = 4
    c: DistanceY(g-1,g22) = 25.5
    c: DistanceX(g-1,g21) = 31
    c: DistanceX(g22,g22) = 100
    c: Coincident(g22,g21)
FEATURE [PartDesign::Pad] Pad001  label="PadFace"
  ClaimChildren = false
  Direction = (1,1,1)
  Fit = 0
  FitJoin = 0
  InnerFit = 0
  InnerFitJoin = 0
  InnerTaperAngle = 0
  InnerTaperAngleRev = 0
  Length = 3
  Length2 = 100
  NewSolid = false
  Placement = pos=(0,0,0) rot=(1,0,0;1.5708rad)
  Profile = -> Sketch033
  Suppress = false
  Type = 0
  expr: Length = <<param>>.face_thickness
FEATURE [PartDesign::Chamfer] Chamfer001
  Angle = 45
  Base = -> Pad001 [Edge34]
  BaseFeature = -> Pad001
  ChamferType = 0
  FlipDirection = false
  NewSolid = false
  Placement = pos=(0,0,0) rot=(1,0,0;1.5708rad)
  Size = 2
  Size2 = 1
  SupportTransform = false
  Suppress = false
FEATURE [PartDesign::Chamfer] Chamfer002
  Angle = 45
  Base = -> Chamfer001 [Edge54,Edge56,Edge53,Edge55]
  BaseFeature = -> Chamfer001
  ChamferType = 0
  FlipDirection = false
  NewSolid = false
  Placement = pos=(0,0,0) rot=(1,0,0;1.5708rad)
  Size = 1.4
  Size2 = 1
  SupportTransform = false
  Suppress = false
FEATURE [Sketcher::SketchObject] Sketch034
  FullyConstrained = true
  MapMode = 5
  Placement = pos=(0,0,0) rot=(1,0,0;1.5708rad)
  Support = -> [XZ_Plane008]
  sketch-geometry (6):
    g0: LineSegment StartX=-1 StartY=6.25 StartZ=0 EndX=1 EndY=6.25 EndZ=0
    g1: LineSegment StartX=1 StartY=6.25 StartZ=0 EndX=1 EndY=7.75 EndZ=0
    g2: LineSegment StartX=1 StartY=7.75 StartZ=0 EndX=0 EndY=7.75 EndZ=0
    g3: LineSegment StartX=0 StartY=7.75 StartZ=0 EndX=0 EndY=8.75 EndZ=0
    g4: LineSegment StartX=0 StartY=8.75 StartZ=0 EndX=-1 EndY=8.75 EndZ=0
    g5: LineSegment StartX=-1 StartY=8.75 StartZ=0 EndX=-1 EndY=6.25 EndZ=0
  constraints (17):
    c: Coincident(g0,g1)
    c: Vertical(g1)
    c: Coincident(g1,g2)
    c: Horizontal(g2)
    c: Coincident(g2,g3)
    c: Vertical(g3)
    c: Coincident(g3,g4)
    c: Horizontal(g4)
    c: Coincident(g4,g5)
    c: Coincident(g5,g0)
    c: Vertical(g5)
    c: DistanceX(g0,g0) = 2
    c: DistanceY(g3,g3) = 1
    c: DistanceX(g4,g4) = 1
    c: Symmetric(g0,g0,g-2)
    c: DistanceY(g-1,g0) = 6.25
    c: DistanceY(g5,g5) = 2.5
FEATURE [PartDesign::Revolution] Revolution001
  Angle = 360
  Axis = (1,0,0)
  Base = (0,0,0)
  ClaimChildren = false
  Fit = 0
  FitJoin = 0
  InnerFit = 0
  InnerFitJoin = 0
  NewSolid = false
  Placement = pos=(0,0,0) rot=(1,0,0;1.5708rad)
  Profile = -> Sketch034
  ReferenceAxis = -> X_Axis008
  Suppress = false
FEATURE [PartDesign::Body] Body006  label="BodyRing"
  AutoGroupSolids = false
  ExportMode = 0
  Group = -> [Sketch034,Revolution001]
  Origin = -> Origin008
  Tip = -> Revolution001
  _ExportChildren = -> [Revolution001]
  _GroupVersion = 1
FEATURE [Part::Box] Box  label="Cube"
  AttacherType = Attacher::AttachEngine3D
  Height = 18
  Length = 18
  Placement = pos=(-9,-0.25,-9) rot=(0,0,1;0rad)
  Width = 0.5
FEATURE [Part::FeaturePython] Slice001  # WARN: FeaturePython — macro-defined, semantics opaque (R4)
  Base = -> Body006
  Mode = 1
  Tolerance = 0
  Tools = -> [Box]
FEATURE [Part::FeaturePython] Slice001_child1  label="Slice001.1"  # WARN: FeaturePython — macro-defined, semantics opaque (R4)
  Base = -> Slice001
  FilterType = 1
  Invert = false
  OverrideMaxVal = 0
  WindowFrom = 80
  WindowTo = 100
  items = 1
FEATURE [Part::FeaturePython] Slice001_child2  label="Slice001.2"  # WARN: FeaturePython — macro-defined, semantics opaque (R4)
  Base = -> Slice001
  FilterType = 1
  Invert = false
  OverrideMaxVal = 0
  WindowFrom = 80
  WindowTo = 100
  items = 2
FEATURE [App::DocumentObjectGroup] GrExplode_Slice001  label="Exploded SliceRing"
  ExportMode = 1
  Group = -> [Slice001_child1,Slice001_child2]
  _GroupVersion = 1
FEATURE [Sketcher::SketchObject] Sketch035
  AttachmentOffset = pos=(0,0,1.5) rot=(1,0,0;0rad)
  ExternalGeometry = -> [Sketch033]
  FullyConstrained = true
  MapMode = 5
  Placement = pos=(0,-1.5,-3e-16) rot=(1,0,0;1.5708rad)
  Support = -> [XZ_Plane007]
  expr: .AttachmentOffset.Base.z = <<param>>.face_thickness - 1.5
  sketch-geometry (1):
    g0: Circle CenterX=-31 CenterY=21.5 CenterZ=0 NormalX=0 NormalY=0 NormalZ=1 AngleXU=0 Radius=9
  constraints (2):
    c: Coincident(g0,g-3)
    c: Diameter(g0) = 18
FEATURE [PartDesign::Pocket] Pocket008
  BaseFeature = -> Chamfer002
  ClaimChildren = false
  Fit = 0
  FitJoin = 0
  InnerFit = 0
  InnerFitJoin = 0
  InnerTaperAngle = 0
  InnerTaperAngleRev = 0
  Length = 1.5
  Length2 = 100
  NewSolid = false
  Placement = pos=(0,0,0) rot=(1,0,0;1.5708rad)
  Profile = -> Sketch035
  Reversed = true
  Suppress = false
  Type = 1
FEATURE [Mesh::Feature] Mesh002  label="Exploded Slice001 (Meshed)"
FEATURE [Sketcher::SketchObject] Sketch036
  ExternalGeometry = -> [Sketch033]
  FullyConstrained = true
  MapMode = 5
  Placement = pos=(0,0,0) rot=(1,0,0;1.5708rad)
  Support = -> [XZ_Plane007]
  sketch-geometry (5):
    g0: ArcOfCircle CenterX=30 CenterY=19.5 CenterZ=0 NormalX=0 NormalY=0 NormalZ=1 AngleXU=0 Radius=0.75 StartAngle=1.5708 EndAngle=4.71239
    g1: ArcOfCircle CenterX=32 CenterY=19.5 CenterZ=0 NormalX=0 NormalY=0 NormalZ=1 AngleXU=0 Radius=0.75 StartAngle=4.71239 EndAngle=7.85398
    g2: LineSegment StartX=30 StartY=18.75 StartZ=0 EndX=32 EndY=18.75 EndZ=0
    g3: LineSegment StartX=30 StartY=20.25 StartZ=0 EndX=32 EndY=20.25 EndZ=0
    g4: LineSegment [constr] StartX=31 StartY=25.5 StartZ=0 EndX=31 EndY=16.5 EndZ=0
  constraints (12):
    c: Tangent(g0,g3) = 1.5708
    c: Tangent(g0,g2) = -1.5708
    c: Tangent(g2,g1) = -1.5708
    c: Tangent(g3,g1) = 1.5708
    c: Horizontal(g2)
    c: Equal(g0,g1)
    c: DistanceY(g1,g-3) = 6
    c: DistanceY(g1,g1) = 1.5
    c: DistanceX(g0,g1) = 2
    c: Coincident(g4,g-3)
    c: Symmetric(g0,g1,g4)
    c: DistanceY(g4,g4) = 9
FEATURE [PartDesign::Pocket] Pocket009
  BaseFeature = -> Pocket008
  ClaimChildren = false
  Fit = 0
  FitJoin = 0
  InnerFit = 0
  InnerFitJoin = 0
  InnerTaperAngle = 0
  InnerTaperAngleRev = 0
  Length = 1
  Length2 = 100
  NewSolid = false
  Placement = pos=(0,0,0) rot=(1,0,0;1.5708rad)
  Profile = -> Sketch036
  Reversed = true
  Suppress = false
  Type = 0
FEATURE [PartDesign::Body] Body005  label="BodyKSGER"
  AutoGroupSolids = false
  ExportMode = 0
  Group = -> [Sketch033,Pad001,Chamfer001,Chamfer002,Sketch035,Pocket008,Sketch036,Pocket009]
  Origin = -> Origin007
  Tip = -> Pocket009
  _ExportChildren = -> [Pad001,Chamfer001,Chamfer002,Pocket008,Pocket009]
  _GroupVersion = 1
FEATURE [Mesh::Feature] Mesh003  label="BodyKSGER (Meshed)"
FEATURE [PartDesign::Fillet] Fillet
  Base = -> Pocket [Edge63,Edge30]
  BaseFeature = -> Pocket
  NewSolid = false
  Radius = 10
  SupportTransform = false
  Suppress = false
  expr: Radius = <<param>>.radius_big
FEATURE [PartDesign::Fillet] Fillet004
  Base = -> Fillet [Edge4]
  BaseFeature = -> Fillet
  NewSolid = false
  Radius = 2.9
  SupportTransform = false
  Suppress = false
FEATURE [PartDesign::Chamfer] Chamfer
  Angle = 45
  Base = -> Fillet004 [Edge9,Edge10,Edge11,Edge25,Edge26]
  BaseFeature = -> Fillet004
  ChamferType = 0
  FlipDirection = false
  NewSolid = false
  Size = 1.4
  Size2 = 1
  SupportTransform = false
  Suppress = false
FEATURE [PartDesign::Body] Body  label="BodyBack"
  AutoGroupSolids = false
  BaseFeature = -> Slice_child1
  ExportMode = 0
  Group = -> [BaseFeature,Sketch032,Pocket,Fillet,Fillet004,Chamfer]
  Origin = -> Origin
  Tip = -> Chamfer
  _ExportChildren = -> [BaseFeature,Pocket,Fillet,Fillet004,Chamfer]
  _GroupVersion = 1
FEATURE [PartDesign::Fillet] Fillet005
  Base = -> Pocket003 [Edge122,Edge190]
  BaseFeature = -> Pocket003
  NewSolid = false
  Radius = 10
  SupportTransform = false
  Suppress = false
  expr: Radius = <<param>>.radius_big
FEATURE [PartDesign::Fillet] Fillet006
  Base = -> Fillet005 [Edge5]
  BaseFeature = -> Fillet005
  NewSolid = false
  Radius = 2
  SupportTransform = false
  Suppress = false
FEATURE [PartDesign::Fillet] Fillet007
  Base = -> Fillet006 [Edge7]
  BaseFeature = -> Fillet006
  NewSolid = false
  Radius = 2
  SupportTransform = false
  Suppress = false
FEATURE [Mesh::Feature] Mesh004  label="BodyBack (Meshed)"
FEATURE [PartDesign::Fillet] Fillet008
  Base = -> Fillet007 [Edge95]
  BaseFeature = -> Fillet007
  NewSolid = false
  Radius = 10
  SupportTransform = false
  Suppress = false
FEATURE [PartDesign::Body] Body004  label="BodyCase"
  AutoGroupSolids = false
  BaseFeature = -> Slice_child0
  ExportMode = 0
  Group = -> [BaseFeature001,Sketch008,Sketch029,Sketch018,Sketch019,Sketch021,Sketch022,Sketch023,Sketch024,Sketch025,Sketch026,Sketch027,Sketch028,Sketch,Pocket001,Pad,Pocket002,Pocket006,Pocket005,SubtractiveLoft,Revolution,Pocket007,Groove,Pocket004,Pocket003,Fillet005,Fillet006,Fillet007,Fillet008]
  Origin = -> Origin005
  Tip = -> Fillet008
  _ExportChildren = -> [BaseFeature001,Pocket001,Pad,Pocket002,Pocket006,Pocket005,SubtractiveLoft,Revolution,Pocket007,Groove,Pocket004,Pocket003,Fillet005,Fillet006,Fillet007,Fillet008]
  _GroupVersion = 1
FEATURE [Mesh::Feature] Mesh  label="BodyCase (Meshed)"
FEATURE [App::DocumentObjectGroup] Group  label="Mesh"
  ExportMode = 1
  Group = -> [Mesh002,Mesh003,Mesh004,Mesh]
  _GroupVersion = 1
FEATURE [App::Part] Part
  ExportMode = 1
  Group = -> [Extrude,Plane002,Common,Sketch012,Loft,Slice_child1,Slice_child0,Slice,GrExplode_Slice,Sketch030,Sketch031,Group001,Spreadsheet,Body,Body004,Body005,Body006,Mesh002,Group,Mesh003,Mesh004,Mesh]
  Origin = -> Origin006
  _ExportChildren = -> [Group001,Spreadsheet,Body,Body004,Body005,Body006,Group]
  _GroupVersion = 1
